# Revit family: Sink-Kitchen-KOHLER-Farmstead-K-21103_1
name_source: partatom
category: Plumbing Fixtures
revit_build: Autodesk Revit 2015 (Build: 20140606_1530(x64)
units: mm (PartAtom-declared; Revit-internal decimal feet)

## types (6) — shared parameters
ADA Compliant = No
Assembly Code = D2010400
CW Connection = No
Cold Water Inlet = Cold Water Inlet
Date Modified = 12/07/2018
Default Elevation = 34 3/8"
Drain Included = No
Finish = Kohler-Enameled_Cast_Iron-0-White
HW Connection = No
Height = 13 15/16"
Hot Water Inlet = Hot Water Inlet
Length = 45"
Manufacturer = KOHLER Co.
MasterFormat 1995 = 15410
MasterFormat 2004 = 22.41.16
Material = Enameled Cast Iron
Product Documentation Link = http://www.us.kohler.com
Product Name = Farmstead
Product Page URL = http://www.us.kohler.com
URL = https://www.us.kohler.com
Vent Connection = No
Waste Connection = Yes
Waste Water Outlet = Waste Water Outlet
Width = 25"

## per-type parameters (varying)
| type | 21103_1 | 21103_2 | 21103_3 | Description | Model | Type | Underside Finish |
| Single faucet hole, black underside, 0-White | Yes | No | No | 45 inch x 25 inch x 9 inch top-mount/wall-mount kitchen sink with single faucet hole, black underside | K-21103-1HP5-0 | 1 | Kohler-Enameled_Cast_Iron-7-Black_Black |
| Single faucet hole, white underside, 0-White | Yes | No | No | 45 inch x 25 inch x 9 inch top-mount/wall-mount kitchen sink with single faucet hole, white underside | K-21103-1HW-0 | 2 | Kohler-Enameled_Cast_Iron-0-White |
| Two faucet hole, black underside, 0-White | No | Yes | No | 45 inch x 25 inch x 9 inch top-mount/wall-mount kitchen sink with two faucet holes, black underside | K-21103-2HP5-0 | 3 | Kohler-Enameled_Cast_Iron-7-Black_Black |
| Two faucet hole, white underside, 0-White | No | Yes | No | 45 inch x 25 inch x 9 inch top-mount/wall-mount kitchen sink with two faucet holes, white underside | K-21103-2HW-0 | 4 | Kohler-Enameled_Cast_Iron-0-White |
| Three faucet hole, black underside, 0-White | No | No | Yes | 45 inch x 25 inch x 9 inch top-mount/wall-mount kitchen sink with three faucet holes, black underside | K-21103-3HP5-0 | 5 | Kohler-Enameled_Cast_Iron-7-Black_Black |
| Three faucet hole, white underside, 0-White | No | No | Yes | 45 inch x 25 inch x 9 inch top-mount/wall-mount kitchen sink with three faucet holes, white underside | K-21103-3HW-0 | 6 | Kohler-Enameled_Cast_Iron-0-White |

## geometry (parser evidence)
native form markers: Sweep x8
no freeform markers — native parametric forms only
